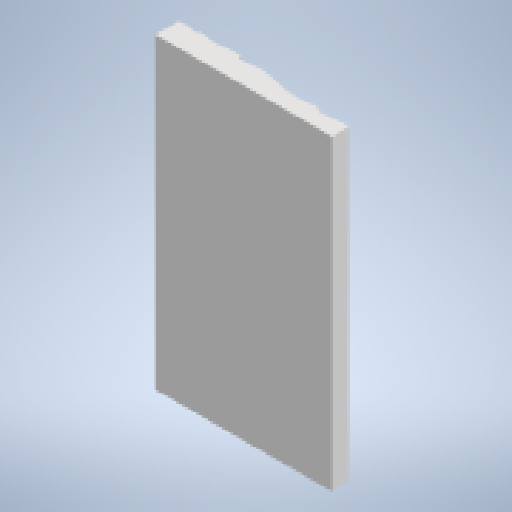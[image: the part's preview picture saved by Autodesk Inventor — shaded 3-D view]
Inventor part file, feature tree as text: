
AUTODESK INVENTOR PART (.ipt)
format: ipt  version: 2023 (Build 270158000, 158)  size: 260,096 bytes
history: native  units: mm
features: reference x6, other x6, extrude x2, sketch x1
ambient origin geometry x8: Origin, YZ Plane, XZ Plane, XY Plane, X Axis, Y Axis, Z Axis, Center Point
bodies: Solid1 (feature_tree)
feature tree (15):
  extrude  "Extrusion1"  Depth=10.0mm
  extrude  "Extrusion5"  Depth=10.0mm TaperAngle=0.0deg
  sketch  "Sketch1"  dims[d3=5.0mm d4=9.75mm d5=0.0mm d6=0.0mm d8=1.0mm d19=202.5mm d20=0.0mm d21=10.0mm d22=0.872665mm d23=0.5mm d24=0.872665mm]
  reference  "Reference1"
  reference  "Reference2"
  reference  "Reference3"
  reference  "Reference4"
  reference  "Reference5"
  reference  "Reference8"
  parser-record x1  (decoder bookkeeping rows leaked as tree rows — omitted from the tree; the rows remain in map.json)
  other  "doorLockAssembly_V4.iam"
  other  "moulding:1"
  other  "rack_V3:1"
  other  "gear_V4:1"
  other  "BallBearing_8x22x7mm:1"
note: 1 file-system path scrubbed to <path> (originals preserved in map.json)
